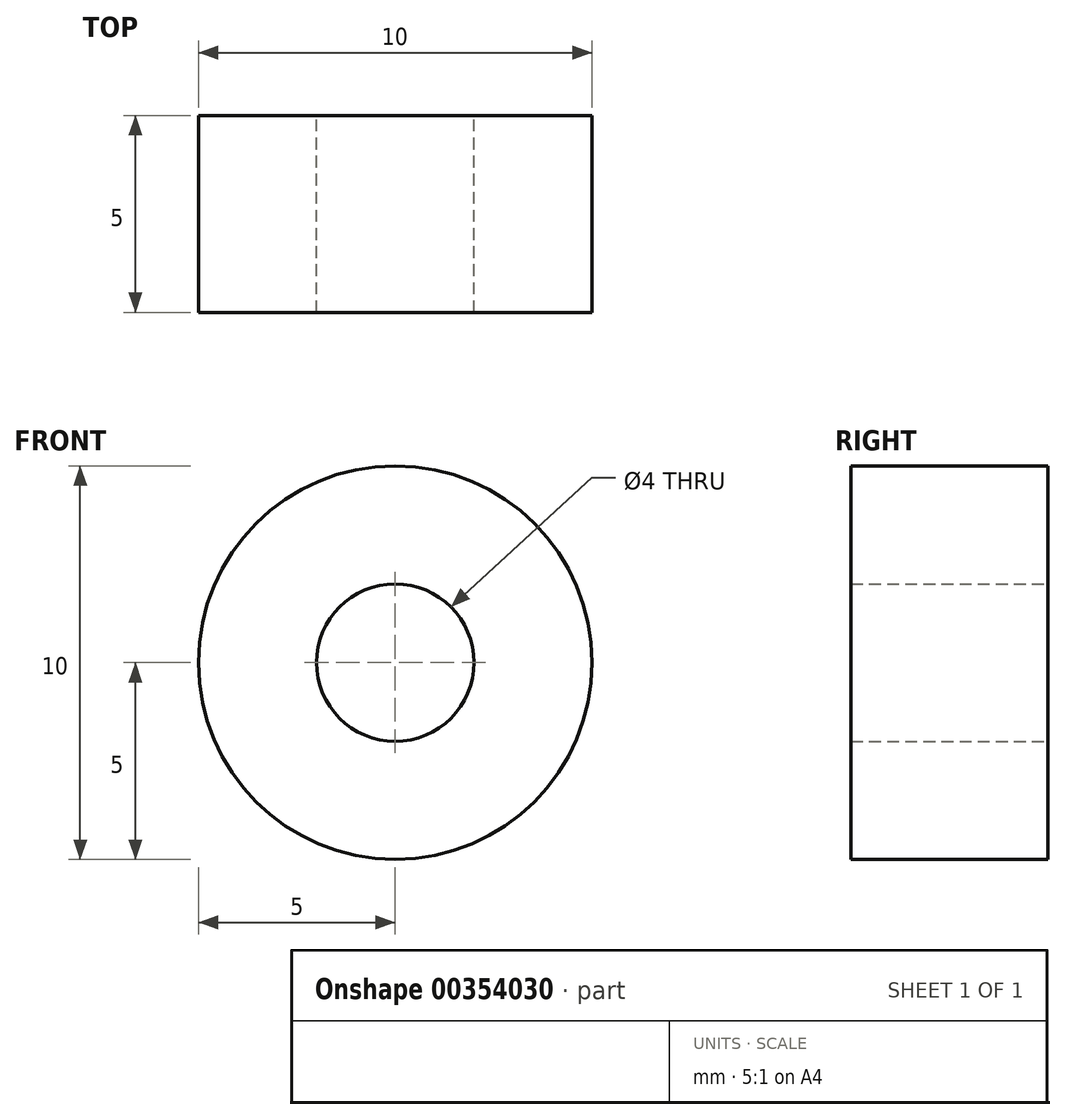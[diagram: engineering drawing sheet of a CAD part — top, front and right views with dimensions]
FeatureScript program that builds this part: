
annotation { "Feature Type Name" : "Feature", "Feature Type Description" : "" }
export const myFeature = defineFeature(function(context is Context, id is Id, definition is map)
    precondition{}
    {
        {
            var Q0;
            Q0=qCreatedBy(makeId("Front.planeOp"),FACE);
            var sketch = newSketch(context, id + "F0", { "sketchPlane" : qUnion([Q0])});
            skCircle(sketch, "E0", {"center": v(0, 0) * mm, "radius": 2 * mm});
            skCircle(sketch, "E1", {"center": v(0, 0) * mm, "radius": 5 * mm});
            skSolve(sketch);
        }
        {
            var Q0;
            Q0=makeQuery(id+"F0.imprint","IMPRINT",FACE,{"disambiguationData":[TD([[makeQuery(id+"F0.imprint","IMPRINT",EDGE,{"derivedFrom":sQuery(id+"F0.wireOp",EDGE,"E0")}),-1.0]])]});
            extrude(context, id + "F1", {"entities" : qUnion([Q0]), "depth" : 5 * mm});
        }
    });
